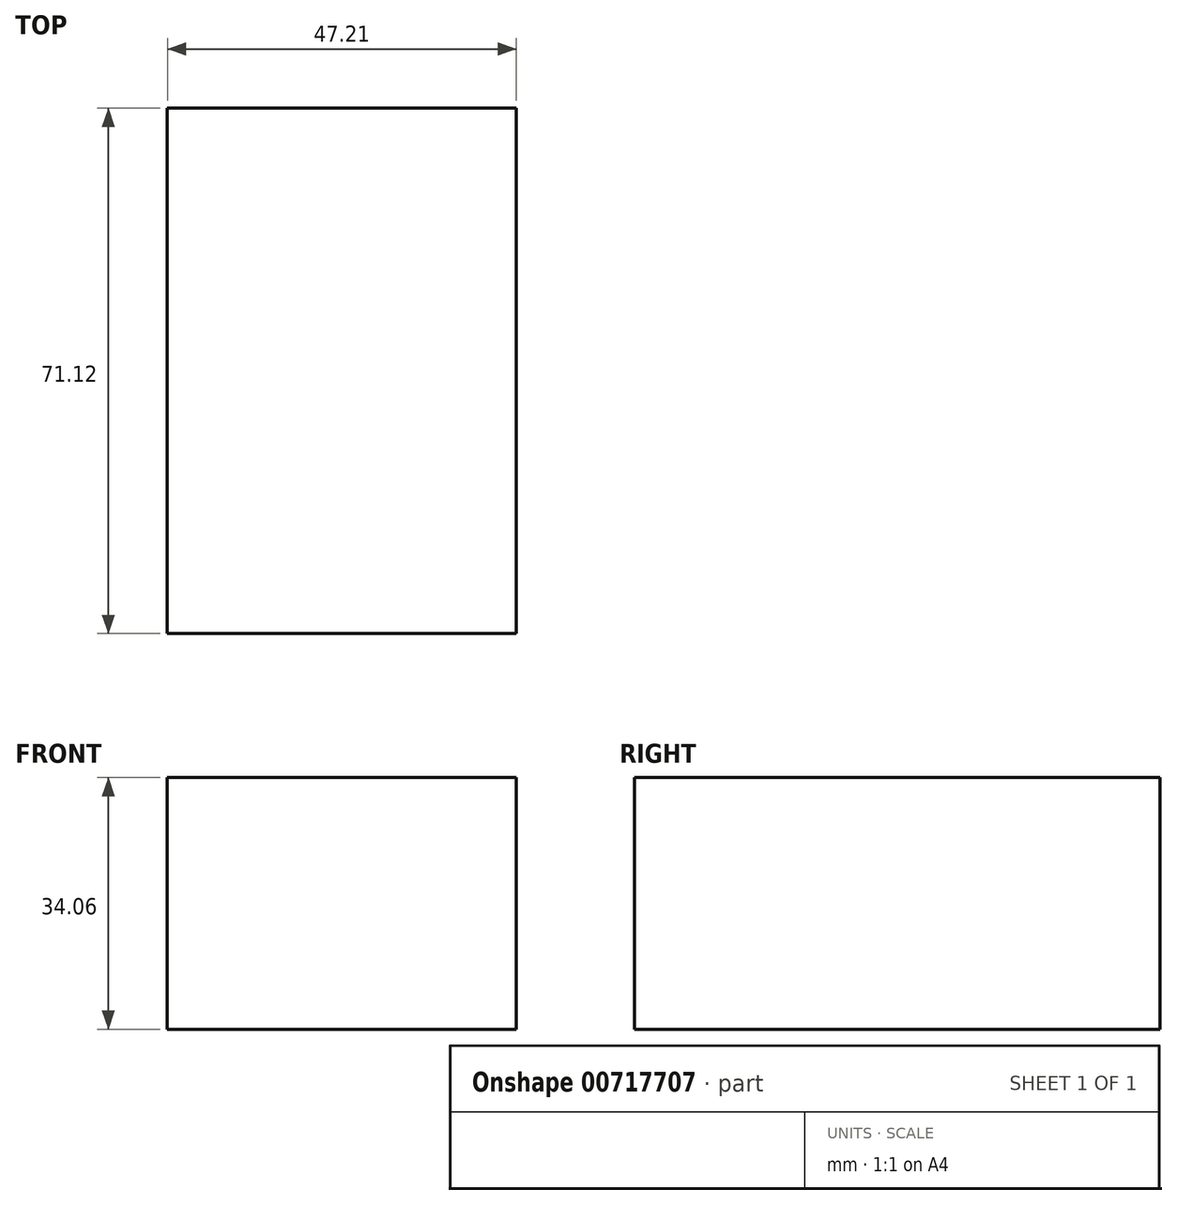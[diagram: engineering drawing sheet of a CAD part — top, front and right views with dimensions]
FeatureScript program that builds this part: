
annotation { "Feature Type Name" : "Feature", "Feature Type Description" : "" }
export const myFeature = defineFeature(function(context is Context, id is Id, definition is map)
    precondition{}
    {
        {
            var Q0;
            Q0=qCreatedBy(makeId("Front.planeOp"),FACE);
            var sketch = newSketch(context, id + "F0", { "sketchPlane" : qUnion([Q0])});
            skCircle(sketch, "E0", {"center": v(7.1, 24.2) * mm, "radius": 66.65 * mm});
            skLineSegment(sketch, "E1.bottom", {"start": v(-47.21, 39.44) * mm, "end": v(0, 39.44) * mm});
            skLineSegment(sketch, "E1.top", {"start": v(-47.21, 5.38) * mm, "end": v(0, 5.38) * mm});
            skLineSegment(sketch, "E1.left", {"start": v(-47.21, 39.44) * mm, "end": v(-47.21, 5.38) * mm});
            skLineSegment(sketch, "E1.right", {"start": v(0, 39.44) * mm, "end": v(0, 5.38) * mm});
            skSolve(sketch);
        }
        {
            var Q0;
            Q0=makeQuery(id+"F0.imprint","IMPRINT",FACE,{"disambiguationData":[TD([[makeQuery(id+"F0.imprint","IMPRINT",EDGE,{"derivedFrom":sQuery(id+"F0.wireOp",EDGE,"E1.bottom")}),-1.0]])]});
            extrude(context, id + "F1", {"entities" : qUnion([Q0]), "depth" : 71.12 * mm, "offsetDistance" : 25.4 * mm});
        }
    });
